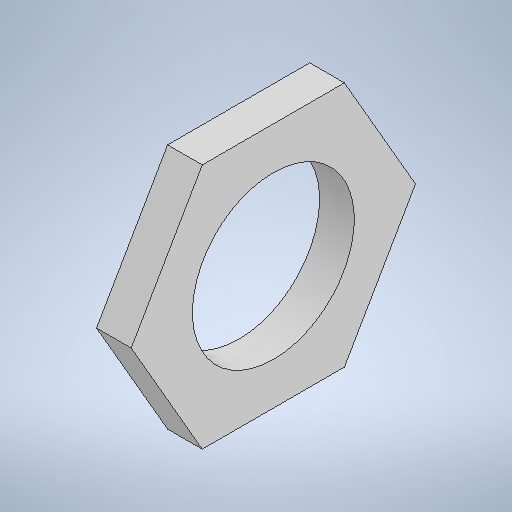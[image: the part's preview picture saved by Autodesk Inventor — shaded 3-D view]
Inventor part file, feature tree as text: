
AUTODESK INVENTOR PART (.ipt)
format: ipt  version: 2025.1 (Build 291241020, 241B)  size: 236,544 bytes
history: native  units: in
note: dims shown in document units (in); Inventor stores cm internally (conversion verified against a paired STEP export)
features: sketch x2, extrude x1
ambient origin geometry x8: Origin, YZ Plane, XZ Plane, XY Plane, X Axis, Y Axis, Z Axis, Center Point
bodies: Body1 (feature_tree)
feature tree (3):
  extrude  "Extrusion2"  Depth=1.0in
  sketch  "Sketch1"  dims[d0=0.56in d1=1.0in]
  sketch  "Sketch Circular Pattern1"  dims[d4=2.3622in d6=360.0deg d8=0.12in d9=0.0in]
